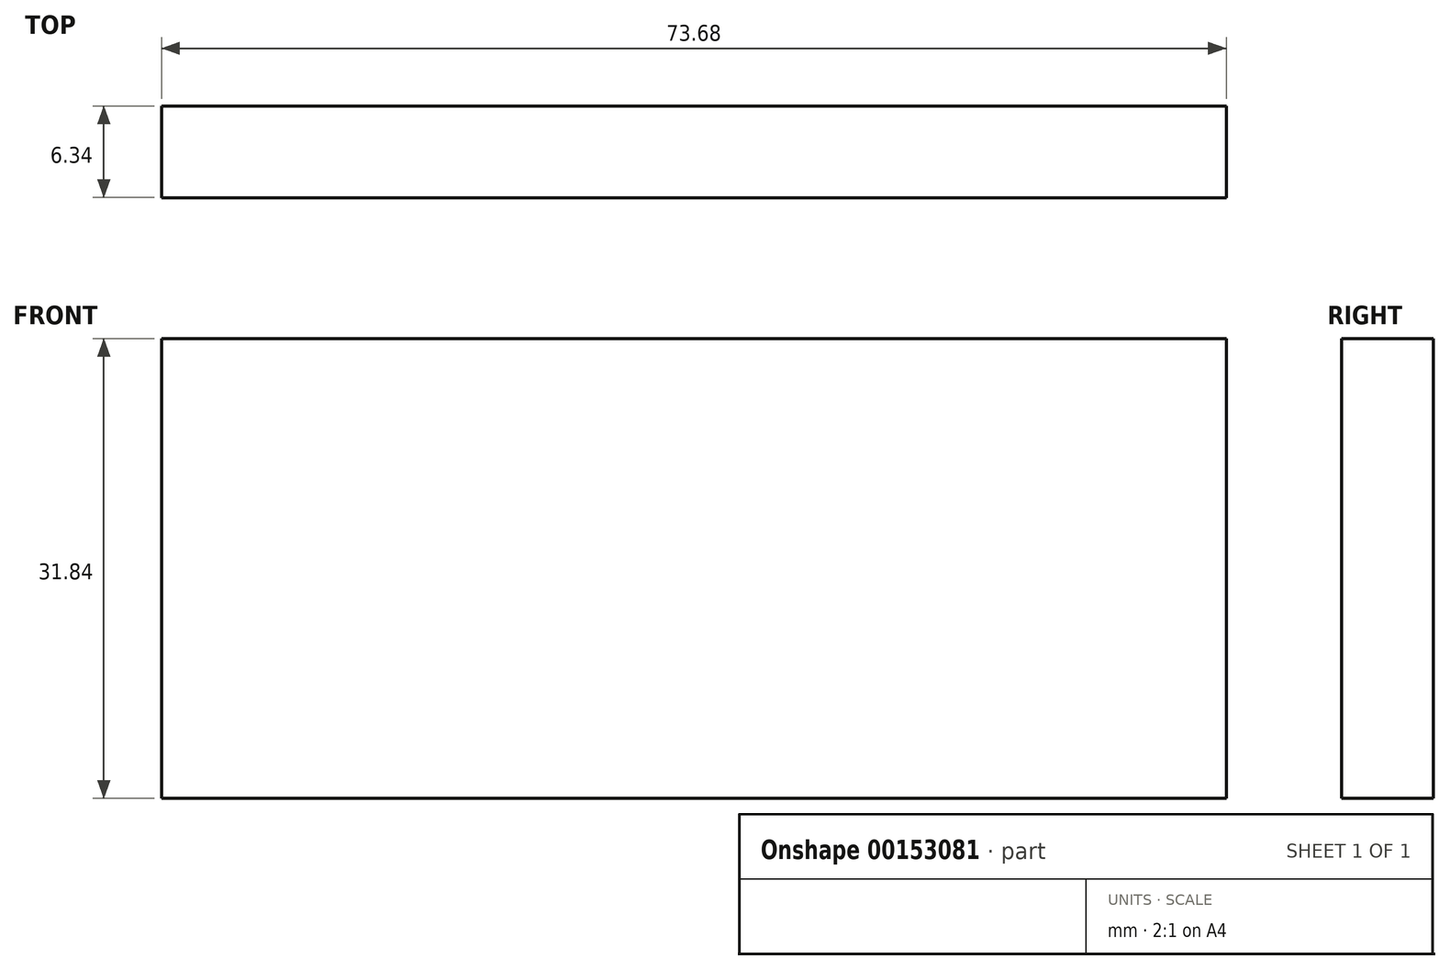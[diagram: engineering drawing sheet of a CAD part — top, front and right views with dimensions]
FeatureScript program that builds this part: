
annotation { "Feature Type Name" : "Feature", "Feature Type Description" : "" }
export const myFeature = defineFeature(function(context is Context, id is Id, definition is map)
    precondition{}
    {
        {
            var Q0;
            Q0=qCreatedBy(makeId("Front.planeOp"),FACE);
            var sketch = newSketch(context, id + "F0", { "sketchPlane" : qUnion([Q0])});
            skLineSegment(sketch, "E0.bottom", {"start": v(36.84, 15.92) * mm, "end": v(-36.84, 15.92) * mm});
            skLineSegment(sketch, "E0.top", {"start": v(36.84, -15.92) * mm, "end": v(-36.84, -15.92) * mm});
            skLineSegment(sketch, "E0.left", {"start": v(36.84, 15.92) * mm, "end": v(36.84, -15.92) * mm});
            skLineSegment(sketch, "E0.right", {"start": v(-36.84, 15.92) * mm, "end": v(-36.84, -15.92) * mm});
            skPoint(sketch, "E0.middle", {"position": v(0, 0) * mm});
            skSolve(sketch);
        }
        {
            var Q0;
            Q0 = qSketchRegion(id + "F0", true);
            extrude(context, id + "F1", {"entities" : qUnion([Q0]), "endBound" : BoundingType.SYMMETRIC, "depth" : 6.35 * mm});
        }
    });
